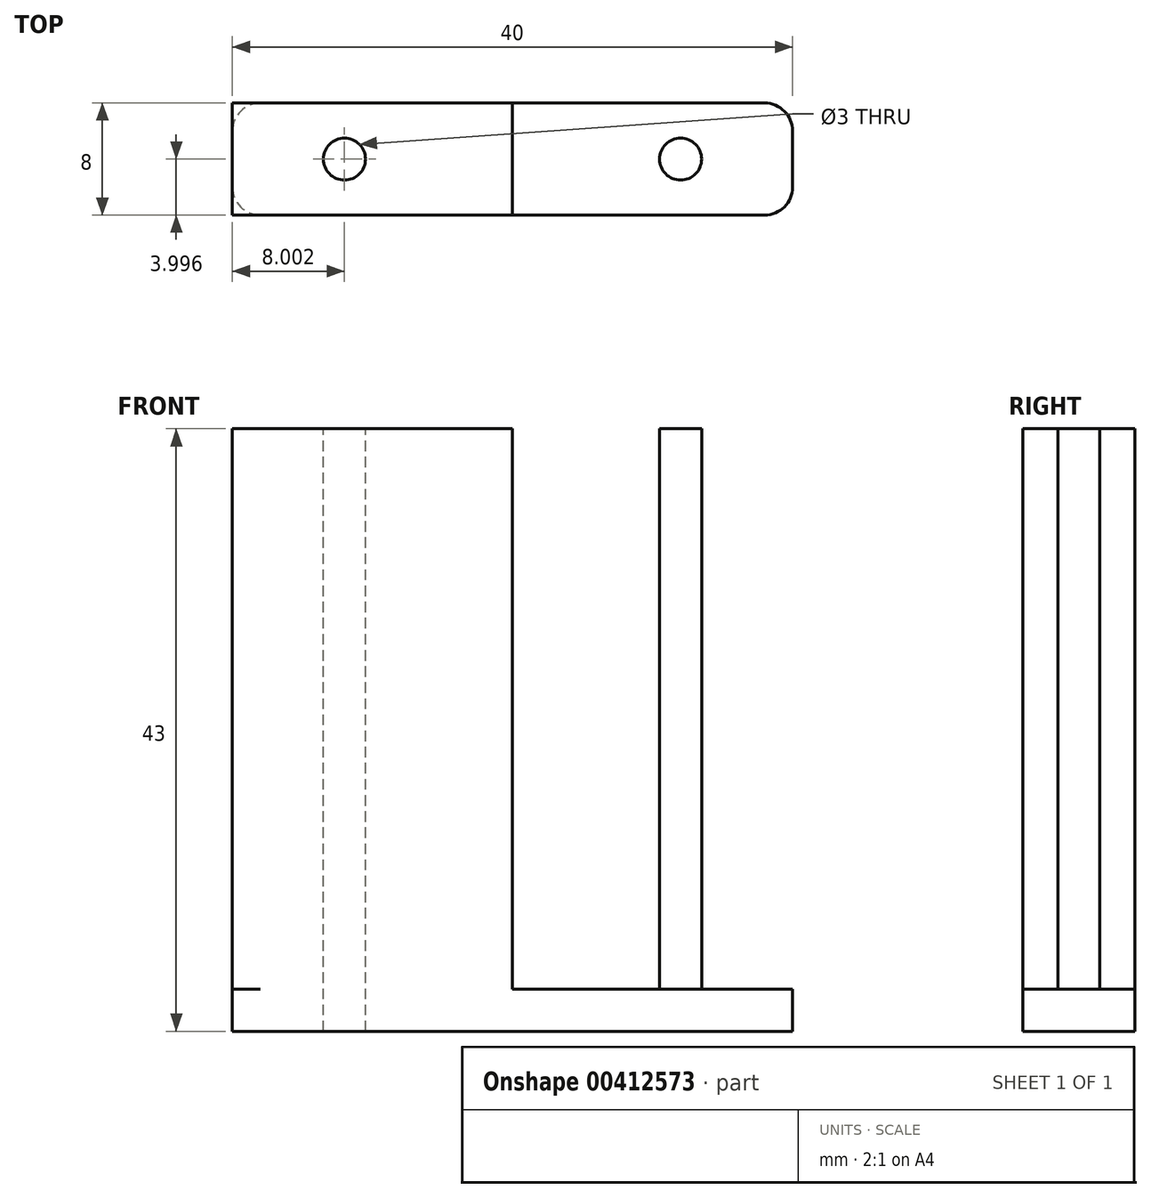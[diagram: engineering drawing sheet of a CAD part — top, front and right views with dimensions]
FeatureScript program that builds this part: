
annotation { "Feature Type Name" : "Feature", "Feature Type Description" : "" }
export const myFeature = defineFeature(function(context is Context, id is Id, definition is map)
    precondition{}
    {
        {
            var Q0;
            Q0=qCreatedBy(makeId("Top.planeOp"),FACE);
            var sketch = newSketch(context, id + "F0", { "sketchPlane" : qUnion([Q0])});
            skLineSegment(sketch, "E0.bottom", {"start": v(-8.27, 4.32) * mm, "end": v(31.73, 4.32) * mm});
            skLineSegment(sketch, "E0.top", {"start": v(-8.27, -3.68) * mm, "end": v(31.73, -3.68) * mm});
            skLineSegment(sketch, "E0.left", {"start": v(-8.27, 4.32) * mm, "end": v(-8.27, -3.68) * mm});
            skLineSegment(sketch, "E0.right", {"start": v(31.73, 4.32) * mm, "end": v(31.73, -3.68) * mm});
            skLineSegment(sketch, "E1", {"start": v(-8.27, 0.32) * mm, "end": v(31.73, 0.32) * mm});
            skLineSegment(sketch, "E2", {"start": v(11.73, 4.32) * mm, "end": v(11.73, -3.68) * mm});
            skCircle(sketch, "E3", {"center": v(-0.27, 0.32) * mm, "radius": 1.5 * mm});
            skCircle(sketch, "E4", {"center": v(23.73, 0.32) * mm, "radius": 1.5 * mm});
            skSolve(sketch);
        }
        {
            var Q0;
            Q0 = qSketchRegion(id + "F0", true);
            var Q1;
            {var subQ0=sQuery(id+"F0.wireOp",EDGE,"E3");var subQ1=sQuery(id+"F0.wireOp",EDGE,"E1");var subQ2=makeQuery(id+"F0.imprint","INTERSECT",VERTEX,{"disambiguationData":[OD(0.0)],"derivedFrom":[subQ1,subQ0]});Q1=makeQuery(id+"F0.imprint","IMPRINT",FACE,{"disambiguationData":[TD([[makeQuery(id+"F0.imprint","IMPRINT",EDGE,{"disambiguationData":[TD([[subQ2,-1.0]])],"derivedFrom":subQ1}),-1.0]])]});}
            var Q2;
            {var subQ0=sQuery(id+"F0.wireOp",EDGE,"E3");var subQ1=sQuery(id+"F0.wireOp",EDGE,"E1");var subQ2=makeQuery(id+"F0.imprint","INTERSECT",VERTEX,{"disambiguationData":[OD(0.0)],"derivedFrom":[subQ1,subQ0]});Q2=makeQuery(id+"F0.imprint","IMPRINT",FACE,{"disambiguationData":[TD([[makeQuery(id+"F0.imprint","IMPRINT",EDGE,{"disambiguationData":[TD([[subQ2,-1.0]])],"derivedFrom":subQ1}),1.0]])]});}
            var Q3;
            {var subQ0=sQuery(id+"F0.wireOp",EDGE,"E4");var subQ1=sQuery(id+"F0.wireOp",EDGE,"E1");var subQ2=makeQuery(id+"F0.imprint","INTERSECT",VERTEX,{"disambiguationData":[OD(0.0)],"derivedFrom":[subQ1,subQ0]});Q3=makeQuery(id+"F0.imprint","IMPRINT",FACE,{"disambiguationData":[TD([[makeQuery(id+"F0.imprint","IMPRINT",EDGE,{"disambiguationData":[TD([[subQ2,-1.0]])],"derivedFrom":subQ1}),1.0]])]});}
            var Q4;
            {var subQ0=sQuery(id+"F0.wireOp",EDGE,"E4");var subQ1=sQuery(id+"F0.wireOp",EDGE,"E1");var subQ2=makeQuery(id+"F0.imprint","INTERSECT",VERTEX,{"disambiguationData":[OD(0.0)],"derivedFrom":[subQ1,subQ0]});Q4=makeQuery(id+"F0.imprint","IMPRINT",FACE,{"disambiguationData":[TD([[makeQuery(id+"F0.imprint","IMPRINT",EDGE,{"disambiguationData":[TD([[subQ2,-1.0]])],"derivedFrom":subQ1}),-1.0]])]});}
            extrude(context, id + "F1", {"entities" : qUnion([Q0, Q1, Q2, Q3, Q4]), "oppositeDirection" : true, "depth" : 3 * mm});
        }
        {
            var Q0;
            Q0=makeQuery(id+"F1.opExtrude","SWEPT_EDGE",EDGE,{"disambiguationData":[OSD([sQuery(id+"F0.wireOp",EDGE,"E0.top"),sQuery(id+"F0.wireOp",EDGE,"E0.left")])]});
            var Q1;
            Q1=makeQuery(id+"F1.opExtrude","SWEPT_EDGE",EDGE,{"disambiguationData":[OSD([sQuery(id+"F0.wireOp",EDGE,"E0.bottom"),sQuery(id+"F0.wireOp",EDGE,"E0.left")])]});
            var Q2;
            Q2=makeQuery(id+"F1.opExtrude","SWEPT_EDGE",EDGE,{"disambiguationData":[OSD([sQuery(id+"F0.wireOp",EDGE,"E0.top"),sQuery(id+"F0.wireOp",EDGE,"E0.right")])]});
            var Q3;
            Q3=makeQuery(id+"F1.opExtrude","SWEPT_EDGE",EDGE,{"disambiguationData":[OSD([sQuery(id+"F0.wireOp",EDGE,"E0.bottom"),sQuery(id+"F0.wireOp",EDGE,"E0.right")])]});
            fillet(context, id + "F2", {"entities" : qUnion([Q0, Q1, Q2, Q3]), "radius" : 2 * mm, "tangentPropagation" : true, "allowEdgeOverflow" : false});
        }
        {
            var Q0;
            {var subQ0=sQuery(id+"F0.wireOp",EDGE,"E3");var subQ1=sQuery(id+"F0.wireOp",EDGE,"E1");var subQ2=makeQuery(id+"F0.imprint","INTERSECT",VERTEX,{"disambiguationData":[OD(0.0)],"derivedFrom":[subQ1,subQ0]});Q0=makeQuery(id+"F0.imprint","IMPRINT",FACE,{"disambiguationData":[TD([[makeQuery(id+"F0.imprint","IMPRINT",EDGE,{"disambiguationData":[TD([[subQ2,-1.0]])],"derivedFrom":subQ1}),1.0]])]});}
            var Q1;
            {var subQ0=sQuery(id+"F0.wireOp",EDGE,"E3");var subQ1=sQuery(id+"F0.wireOp",EDGE,"E1");var subQ2=makeQuery(id+"F0.imprint","INTERSECT",VERTEX,{"disambiguationData":[OD(0.0)],"derivedFrom":[subQ1,subQ0]});Q1=makeQuery(id+"F0.imprint","IMPRINT",FACE,{"disambiguationData":[TD([[makeQuery(id+"F0.imprint","IMPRINT",EDGE,{"disambiguationData":[TD([[subQ2,-1.0]])],"derivedFrom":subQ1}),-1.0]])]});}
            var Q2;
            {var subQ0=sQuery(id+"F0.wireOp",EDGE,"E4");var subQ1=sQuery(id+"F0.wireOp",EDGE,"E1");var subQ2=makeQuery(id+"F0.imprint","INTERSECT",VERTEX,{"disambiguationData":[OD(0.0)],"derivedFrom":[subQ1,subQ0]});Q2=makeQuery(id+"F0.imprint","IMPRINT",FACE,{"disambiguationData":[TD([[makeQuery(id+"F0.imprint","IMPRINT",EDGE,{"disambiguationData":[TD([[subQ2,-1.0]])],"derivedFrom":subQ1}),1.0]])]});}
            var Q3;
            {var subQ0=sQuery(id+"F0.wireOp",EDGE,"E4");var subQ1=sQuery(id+"F0.wireOp",EDGE,"E1");var subQ2=makeQuery(id+"F0.imprint","INTERSECT",VERTEX,{"disambiguationData":[OD(0.0)],"derivedFrom":[subQ1,subQ0]});Q3=makeQuery(id+"F0.imprint","IMPRINT",FACE,{"disambiguationData":[TD([[makeQuery(id+"F0.imprint","IMPRINT",EDGE,{"disambiguationData":[TD([[subQ2,-1.0]])],"derivedFrom":subQ1}),-1.0]])]});}
            extrude(context, id + "F3", {"entities" : qUnion([Q0, Q1, Q2, Q3]), "operationType" : NewBodyOperationType.ADD, "depth" : 40 * mm});
        }
    });
